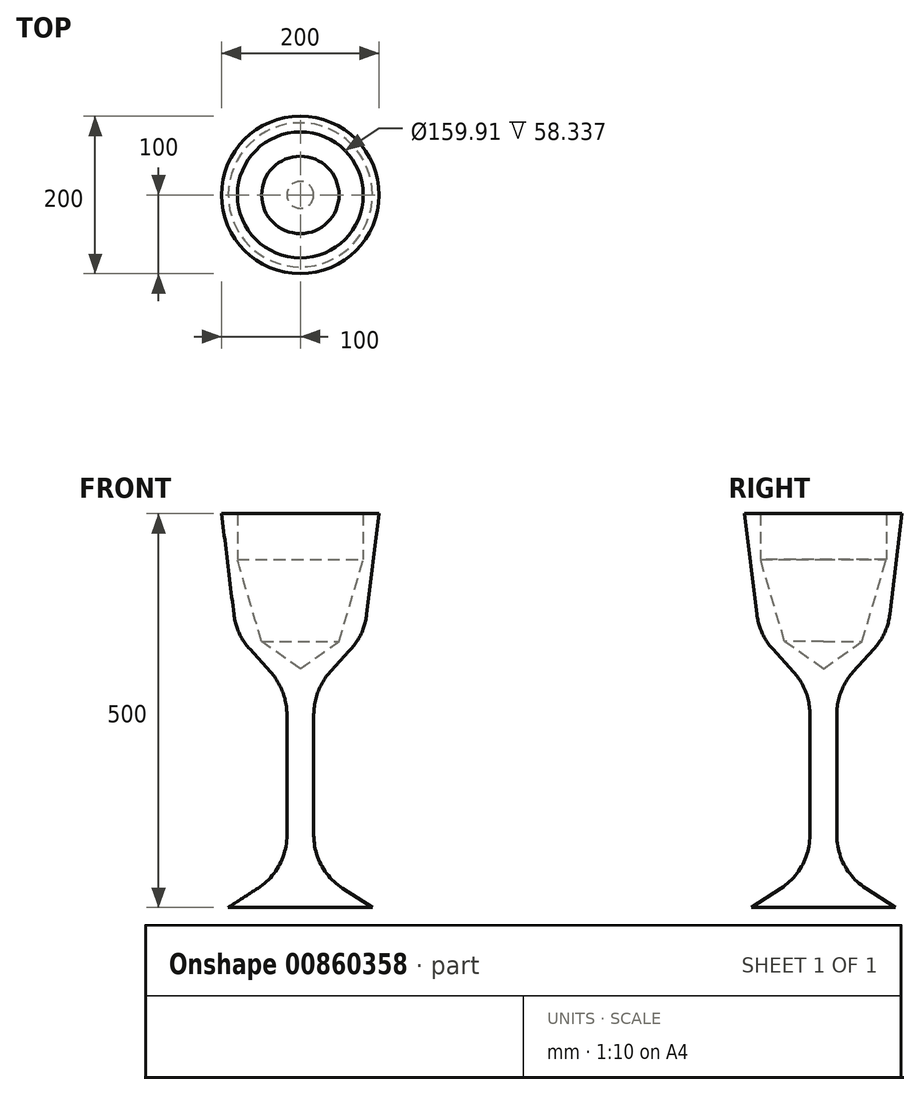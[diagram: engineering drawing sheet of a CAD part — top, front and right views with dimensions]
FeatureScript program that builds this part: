
annotation { "Feature Type Name" : "Feature", "Feature Type Description" : "" }
export const myFeature = defineFeature(function(context is Context, id is Id, definition is map)
    precondition{}
    {
        {
            var Q0;
            Q0=qCreatedBy(makeId("Front.planeOp"),FACE);
            var sketch = newSketch(context, id + "F0", { "sketchPlane" : qUnion([Q0])});
            skLineSegment(sketch, "E0", {"start": v(0, 500) * mm, "end": v(100, 500) * mm});
            skLineSegment(sketch, "E1", {"start": v(0, 0) * mm, "end": v(91.5, 0) * mm});
            skLineSegment(sketch, "E2", {"start": v(91.5, 0) * mm, "end": v(17.1, 47.85) * mm});
            skLineSegment(sketch, "E3", {"start": v(17.1, 47.85) * mm, "end": v(17.1, 276.06) * mm});
            skLineSegment(sketch, "E4", {"start": v(17.1, 276.06) * mm, "end": v(81.24, 346.74) * mm});
            skLineSegment(sketch, "E5", {"start": v(81.24, 346.74) * mm, "end": v(100, 500) * mm});
            skLineSegment(sketch, "E6", {"start": v(0, 0) * mm, "end": v(0, 303.12) * mm});
            skLineSegment(sketch, "E7", {"start": v(0, 303.12) * mm, "end": v(49.17, 337.76) * mm});
            skLineSegment(sketch, "E8", {"start": v(49.17, 337.76) * mm, "end": v(79.95, 441.66) * mm});
            skLineSegment(sketch, "E9", {"start": v(79.95, 441.66) * mm, "end": v(79.95, 500) * mm});
            skSolve(sketch);
        }
        {
            var Q0;
            Q0 = qSketchRegion(id + "F0", true);
            var Q1;
            Q1=sQuery(id+"F0.wireOp",EDGE,"E6");
            revolve(context, id + "F1", {"surfaceOperationType" : NewSurfaceOperationType.NEW, "entities" : qUnion([Q0]), "axis" : qUnion([Q1]), "revolveType" : RevolveType.FULL});
        }
        {
            var Q0;
            Q0=makeQuery(id+"F1.opRevolve","SWEPT_EDGE",EDGE,{"disambiguationData":[OSD([sQuery(id+"F0.wireOp",EDGE,"E4"),sQuery(id+"F0.wireOp",EDGE,"E5")])]});
            var Q1;
            Q1=makeQuery(id+"F1.opRevolve","SWEPT_EDGE",EDGE,{"disambiguationData":[OSD([sQuery(id+"F0.wireOp",EDGE,"E3"),sQuery(id+"F0.wireOp",EDGE,"E4")])]});
            var Q2;
            Q2=makeQuery(id+"F1.opRevolve","SWEPT_EDGE",EDGE,{"disambiguationData":[OSD([sQuery(id+"F0.wireOp",EDGE,"E2"),sQuery(id+"F0.wireOp",EDGE,"E3")])]});
            fillet(context, id + "F2", {"entities" : qUnion([Q0, Q1, Q2]), "radius" : 80 * mm, "tangentPropagation" : true, "allowEdgeOverflow" : false});
        }
    });
